FCSTD DOCUMENT  (FreeCAD 0.21R33771 (Git))
Label: StudioPosizioneIngranaggiFilettatura
License: All rights reserved
LicenseURL: http://en.wikipedia.org/wiki/All_rights_reserved
objects: Sketcher::SketchObject×13, PartDesign::Body×1
note: 14 computed .brp shape members not serialized (recipe doc carries the construction recipe); baked Part::Feature solids carry a one-line shape summary decoded from their .brp

FEATURE [Sketcher::SketchObject] Sketch
  FullyConstrained = false
  MapMode = 5
  Support = -> [XY_Plane]
  sketch-geometry (8):
    g0: LineSegment StartX=-130 StartY=161.215 StartZ=0 EndX=-130 EndY=148.136 EndZ=0
    g1: LineSegment StartX=-137.541 StartY=155 StartZ=0 EndX=-124.899 EndY=155 EndZ=0
    g2: Circle CenterX=-130 CenterY=155 CenterZ=0 NormalX=0 NormalY=0 NormalZ=1 AngleXU=0 Radius=17.5
    g3: Circle CenterX=-84.1606 CenterY=129.385 CenterZ=0 NormalX=0 NormalY=0 NormalZ=1 AngleXU=0 Radius=35
    g4: Circle CenterX=-54.3551 CenterY=94.9479 CenterZ=0 NormalX=0 NormalY=0 NormalZ=1 AngleXU=0 Radius=30
    g5: Circle CenterX=0 CenterY=0 CenterZ=0 NormalX=0 NormalY=0 NormalZ=1 AngleXU=0 Radius=16.0185
    g6: Circle CenterX=-84.1606 CenterY=129.385 CenterZ=0 NormalX=0 NormalY=0 NormalZ=1 AngleXU=0 Radius=15
    g7: Circle CenterX=-5.98814 CenterY=50.9759 CenterZ=0 NormalX=0 NormalY=0 NormalZ=1 AngleXU=0 Radius=35
  constraints (13):
    c: Vertical(g0)
    c: Horizontal(g1)
    c: DistanceX(g0,g-1) = 130
    c: PointOnObject(g2,g0)
    c: DistanceY(g-1,g1) = 155
    c: PointOnObject(g2,g1)
    c: Radius(g2) = 17.5
    c: Radius(g3) = 35
    c: Coincident(g5,g-1)
    c: Coincident(g6,g3)
    c: Radius(g6) = 15
    c: Radius(g4) = 30
    c: Radius(g7) = 35
FEATURE [Sketcher::SketchObject] Sketch001  label="Sketch0_2"
  FullyConstrained = false
  MapMode = 5
  sketch-geometry (10):
    g0: LineSegment StartX=-130 StartY=161.215 StartZ=0 EndX=-130 EndY=148.136 EndZ=0
    g1: LineSegment StartX=-137.541 StartY=155 StartZ=0 EndX=-124.899 EndY=155 EndZ=0
    g2: Circle CenterX=-130 CenterY=155 CenterZ=0 NormalX=0 NormalY=0 NormalZ=1 AngleXU=0 Radius=22
    g3: Circle CenterX=-79.8283 CenterY=111.953 CenterZ=0 NormalX=0 NormalY=0 NormalZ=1 AngleXU=0 Radius=44
    g4: Circle CenterX=-54.5871 CenterY=76.5539 CenterZ=0 NormalX=0 NormalY=0 NormalZ=1 AngleXU=0 Radius=31.25
    g5: Circle CenterX=0 CenterY=0 CenterZ=0 NormalX=0 NormalY=0 NormalZ=1 AngleXU=0 Radius=19
    g6: Circle CenterX=-79.8283 CenterY=111.953 CenterZ=0 NormalX=0 NormalY=0 NormalZ=1 AngleXU=0 Radius=12.5
    g7: Circle CenterX=-29.1528 CenterY=40.8844 CenterZ=0 NormalX=0 NormalY=0 NormalZ=1 AngleXU=0 Radius=31
    g8: Circle CenterX=-54.5871 CenterY=76.5539 CenterZ=0 NormalX=0 NormalY=0 NormalZ=1 AngleXU=0 Radius=12.5
    g9: LineSegment StartX=-79.8283 StartY=111.953 StartZ=0 EndX=0 EndY=0 EndZ=0
  constraints (20):
    c: Vertical(g0)
    c: Horizontal(g1)
    c: DistanceX(g0,g-1) = 130
    c: PointOnObject(g2,g0)
    c: DistanceY(g-1,g1) = 155
    c: PointOnObject(g2,g1)
    c: Radius(g2) = 22
    c: Radius(g3) = 44
    c: Coincident(g5,g-1)
    c: Coincident(g6,g3)
    c: Radius(g6) = 12.5
    c: Radius(g4) = 31.25
    c: Radius(g7) = 31
    c: Coincident(g8,g4)
    c: Radius(g8) = 12.5
    c: Radius(g5) = 19
    c: Coincident(g9,g3)
    c: Coincident(g9,g5)
    c: PointOnObject(g4,g9)
    c: PointOnObject(g7,g9)
FEATURE [Sketcher::SketchObject] Sketch002  label="Sketch0_25"
  FullyConstrained = false
  MapMode = 5
  sketch-geometry (10):
    g0: LineSegment StartX=-130 StartY=161.215 StartZ=0 EndX=-130 EndY=148.136 EndZ=0
    g1: LineSegment StartX=-137.541 StartY=155 StartZ=0 EndX=-124.899 EndY=155 EndZ=0
    g2: Circle CenterX=-130 CenterY=155 CenterZ=0 NormalX=0 NormalY=0 NormalZ=1 AngleXU=0 Radius=22
    g3: Circle CenterX=-69.3987 CenterY=116.141 CenterZ=0 NormalX=0 NormalY=0 NormalZ=1 AngleXU=0 Radius=50
    g4: Circle CenterX=-36.9263 CenterY=61.7972 CenterZ=0 NormalX=0 NormalY=0 NormalZ=1 AngleXU=0 Radius=44
    g5: Circle CenterX=0 CenterY=0 CenterZ=0 NormalX=0 NormalY=0 NormalZ=1 AngleXU=0 Radius=19
    g6: Circle CenterX=-69.3987 CenterY=116.141 CenterZ=0 NormalX=0 NormalY=0 NormalZ=1 AngleXU=0 Radius=19
    g7: Circle CenterX=-20.1669 CenterY=33.7498 CenterZ=0 NormalX=0 NormalY=0 NormalZ=1 AngleXU=0 Radius=20
    g8: Circle CenterX=-36.9263 CenterY=61.7972 CenterZ=0 NormalX=0 NormalY=0 NormalZ=1 AngleXU=0 Radius=12.5
    g9: LineSegment StartX=-69.3987 StartY=116.141 StartZ=0 EndX=0 EndY=0 EndZ=0
  constraints (21):
    c: Vertical(g0)
    c: Horizontal(g1)
    c: DistanceX(g0,g-1) = 130
    c: PointOnObject(g2,g0)
    c: DistanceY(g-1,g1) = 155
    c: PointOnObject(g2,g1)
    c: Radius(g2) = 22
    c: Radius(g3) = 50
    c: Coincident(g5,g-1)
    c: Coincident(g6,g3)
    c: Radius(g6) = 19
    c: Radius(g4) = 44
    c: Radius(g7) = 20
    c: Coincident(g8,g4)
    c: Radius(g8) = 12.5
    c: Radius(g5) = 19
    c: Coincident(g9,g3)
    c: Coincident(g9,g5)
    c: PointOnObject(g4,g9)
    c: PointOnObject(g7,g9)
    c: Angle(g-1,g9) = 2.1094
FEATURE [Sketcher::SketchObject] Sketch003  label="Sketch0_50"
  FullyConstrained = false
  MapMode = 5
  sketch-geometry (10):
    g0: LineSegment StartX=-130 StartY=161.215 StartZ=0 EndX=-130 EndY=148.136 EndZ=0
    g1: LineSegment StartX=-137.541 StartY=155 StartZ=0 EndX=-124.899 EndY=155 EndZ=0
    g2: Circle CenterX=-130 CenterY=155 CenterZ=0 NormalX=0 NormalY=0 NormalZ=1 AngleXU=0 Radius=22
    g3: Circle CenterX=-65.5057 CenterY=123.377 CenterZ=0 NormalX=0 NormalY=0 NormalZ=1 AngleXU=0 Radius=50
    g4: Circle CenterX=-35.8708 CenterY=67.5609 CenterZ=0 NormalX=0 NormalY=0 NormalZ=1 AngleXU=0 Radius=44
    g5: Circle CenterX=0 CenterY=0 CenterZ=0 NormalX=0 NormalY=0 NormalZ=1 AngleXU=0 Radius=19
    g6: Circle CenterX=-65.5057 CenterY=123.377 CenterZ=0 NormalX=0 NormalY=0 NormalZ=1 AngleXU=0 Radius=19
    g7: Circle CenterX=-35.8708 CenterY=67.5609 CenterZ=0 NormalX=0 NormalY=0 NormalZ=1 AngleXU=0 Radius=25
    g8: LineSegment StartX=-65.5057 StartY=123.377 StartZ=0 EndX=0 EndY=0 EndZ=0
    g9: Circle CenterX=-16.4847 CenterY=31.0482 CenterZ=0 NormalX=0 NormalY=0 NormalZ=1 AngleXU=0 Radius=16
  constraints (20):
    c: Vertical(g0)
    c: Horizontal(g1)
    c: DistanceX(g0,g-1) = 130
    c: PointOnObject(g2,g0)
    c: DistanceY(g-1,g1) = 155
    c: PointOnObject(g2,g1)
    c: Radius(g2) = 22
    c: Radius(g3) = 50
    c: Coincident(g5,g-1)
    c: Coincident(g6,g3)
    c: Radius(g6) = 19
    c: Radius(g4) = 44
    c: Coincident(g7,g4)
    c: Radius(g7) = 25
    c: Radius(g5) = 19
    c: Coincident(g8,g3)
    c: PointOnObject(g4,g8)
    c: Coincident(g8,g5)
    c: PointOnObject(g9,g8)
    c: Radius(g9) = 16
FEATURE [Sketcher::SketchObject] Sketch004  label="Sketch0_75"
  FullyConstrained = false
  MapMode = 5
  sketch-geometry (10):
    g0: LineSegment StartX=-130 StartY=161.215 StartZ=0 EndX=-130 EndY=148.136 EndZ=0
    g1: LineSegment StartX=-137.541 StartY=155 StartZ=0 EndX=-124.899 EndY=155 EndZ=0
    g2: Circle CenterX=-130 CenterY=155 CenterZ=0 NormalX=0 NormalY=0 NormalZ=1 AngleXU=0 Radius=22
    g3: Circle CenterX=-79.3893 CenterY=104.018 CenterZ=0 NormalX=0 NormalY=0 NormalZ=1 AngleXU=0 Radius=50
    g4: Circle CenterX=-51.6904 CenterY=67.7259 CenterZ=0 NormalX=0 NormalY=0 NormalZ=1 AngleXU=0 Radius=26
    g5: Circle CenterX=0 CenterY=0 CenterZ=0 NormalX=0 NormalY=0 NormalZ=1 AngleXU=0 Radius=19
    g6: Circle CenterX=-79.3893 CenterY=104.018 CenterZ=0 NormalX=0 NormalY=0 NormalZ=1 AngleXU=0 Radius=19
    g7: Circle CenterX=-51.6904 CenterY=67.7259 CenterZ=0 NormalX=0 NormalY=0 NormalZ=1 AngleXU=0 Radius=5
    g8: LineSegment StartX=-79.3893 StartY=104.018 StartZ=0 EndX=0 EndY=0 EndZ=0
    g9: Circle CenterX=-23.8875 CenterY=31.2979 CenterZ=0 NormalX=0 NormalY=0 NormalZ=1 AngleXU=0 Radius=20
  constraints (20):
    c: Vertical(g0)
    c: Horizontal(g1)
    c: DistanceX(g0,g-1) = 130
    c: PointOnObject(g2,g0)
    c: DistanceY(g-1,g1) = 155
    c: PointOnObject(g2,g1)
    c: Radius(g2) = 22
    c: Radius(g3) = 50
    c: Coincident(g5,g-1)
    c: Coincident(g6,g3)
    c: Radius(g6) = 19
    c: Radius(g4) = 26
    c: Coincident(g7,g4)
    c: Radius(g7) = 5
    c: Radius(g5) = 19
    c: Coincident(g8,g3)
    c: PointOnObject(g4,g8)
    c: Coincident(g8,g5)
    c: PointOnObject(g9,g8)
    c: Radius(g9) = 20
FEATURE [Sketcher::SketchObject] Sketch005  label="Sketch0_8"
  FullyConstrained = false
  MapMode = 5
  sketch-geometry (10):
    g0: LineSegment StartX=-130 StartY=161.215 StartZ=0 EndX=-130 EndY=148.136 EndZ=0
    g1: LineSegment StartX=-137.541 StartY=155 StartZ=0 EndX=-124.899 EndY=155 EndZ=0
    g2: Circle CenterX=-130 CenterY=155 CenterZ=0 NormalX=0 NormalY=0 NormalZ=1 AngleXU=0 Radius=22
    g3: Circle CenterX=-71.9427 CenterY=124.555 CenterZ=0 NormalX=0 NormalY=0 NormalZ=1 AngleXU=0 Radius=43.75
    g4: Circle CenterX=-50.103 CenterY=86.744 CenterZ=0 NormalX=0 NormalY=0 NormalZ=1 AngleXU=0 Radius=31.25
    g5: Circle CenterX=0 CenterY=0 CenterZ=0 NormalX=0 NormalY=0 NormalZ=1 AngleXU=0 Radius=19
    g6: Circle CenterX=-71.9427 CenterY=124.555 CenterZ=0 NormalX=0 NormalY=0 NormalZ=1 AngleXU=0 Radius=12.5
    g7: Circle CenterX=-50.103 CenterY=86.744 CenterZ=0 NormalX=0 NormalY=0 NormalZ=1 AngleXU=0 Radius=5
    g8: LineSegment StartX=-71.9427 StartY=124.555 StartZ=0 EndX=0 EndY=0 EndZ=0
    g9: Circle CenterX=-21.9555 CenterY=38.012 CenterZ=0 NormalX=0 NormalY=0 NormalZ=1 AngleXU=0 Radius=25
  constraints (20):
    c: Vertical(g0)
    c: Horizontal(g1)
    c: DistanceX(g0,g-1) = 130
    c: PointOnObject(g2,g0)
    c: DistanceY(g-1,g1) = 155
    c: PointOnObject(g2,g1)
    c: Radius(g2) = 22
    c: Radius(g3) = 43.75
    c: Coincident(g5,g-1)
    c: Coincident(g6,g3)
    c: Radius(g6) = 12.5
    c: Radius(g4) = 31.25
    c: Coincident(g7,g4)
    c: Radius(g7) = 5
    c: Radius(g5) = 19
    c: Coincident(g8,g3)
    c: PointOnObject(g4,g8)
    c: Coincident(g8,g5)
    c: PointOnObject(g9,g8)
    c: Radius(g9) = 25
FEATURE [Sketcher::SketchObject] Sketch006  label="Sketch_1_0"
  FullyConstrained = false
  MapMode = 5
  sketch-geometry (10):
    g0: LineSegment StartX=-130 StartY=161.215 StartZ=0 EndX=-130 EndY=148.136 EndZ=0
    g1: LineSegment StartX=-137.541 StartY=155 StartZ=0 EndX=-124.899 EndY=155 EndZ=0
    g2: Circle CenterX=-130 CenterY=155 CenterZ=0 NormalX=0 NormalY=0 NormalZ=1 AngleXU=0 Radius=22
    g3: Circle CenterX=-78.399 CenterY=113.861 CenterZ=0 NormalX=0 NormalY=0 NormalZ=1 AngleXU=0 Radius=43.75
    g4: Circle CenterX=-46.27 CenterY=67.1995 CenterZ=0 NormalX=0 NormalY=0 NormalZ=1 AngleXU=0 Radius=37.5
    g5: Circle CenterX=0 CenterY=-1.42e-14 CenterZ=0 NormalX=0 NormalY=0 NormalZ=1 AngleXU=0 Radius=19
    g6: Circle CenterX=-78.399 CenterY=113.861 CenterZ=0 NormalX=0 NormalY=0 NormalZ=1 AngleXU=0 Radius=18.75
    g7: Circle CenterX=-46.27 CenterY=67.1995 CenterZ=0 NormalX=0 NormalY=0 NormalZ=1 AngleXU=0 Radius=5
    g8: LineSegment StartX=-78.399 StartY=113.861 StartZ=0 EndX=0 EndY=-1.42e-14 EndZ=0
    g9: Circle CenterX=-17.8364 CenterY=25.9045 CenterZ=0 NormalX=0 NormalY=0 NormalZ=1 AngleXU=0 Radius=12.5
  constraints (20):
    c: Vertical(g0)
    c: Horizontal(g1)
    c: DistanceX(g0,g-1) = 130
    c: PointOnObject(g2,g0)
    c: DistanceY(g-1,g1) = 155
    c: PointOnObject(g2,g1)
    c: Radius(g2) = 22
    c: Radius(g3) = 43.75
    c: Coincident(g5,g-1)
    c: Coincident(g6,g3)
    c: Radius(g6) = 18.75
    c: Radius(g4) = 37.5
    c: Coincident(g7,g4)
    c: Radius(g7) = 5
    c: Radius(g5) = 19
    c: Coincident(g8,g3)
    c: PointOnObject(g4,g8)
    c: Coincident(g8,g5)
    c: PointOnObject(g9,g8)
    c: Radius(g9) = 12.5
FEATURE [Sketcher::SketchObject] Sketch007  label="Sketch_1_25"
  FullyConstrained = false
  MapMode = 5
  sketch-geometry (10):
    g0: LineSegment StartX=-130 StartY=161.215 StartZ=0 EndX=-130 EndY=148.136 EndZ=0
    g1: LineSegment StartX=-137.541 StartY=155 StartZ=0 EndX=-124.899 EndY=155 EndZ=0
    g2: Circle CenterX=-130 CenterY=155 CenterZ=0 NormalX=0 NormalY=0 NormalZ=1 AngleXU=0 Radius=22
    g3: Circle CenterX=-68.136 CenterY=133.379 CenterZ=0 NormalX=0 NormalY=0 NormalZ=1 AngleXU=0 Radius=43.75
    g4: Circle CenterX=-38.4892 CenterY=75.3442 CenterZ=0 NormalX=0 NormalY=0 NormalZ=1 AngleXU=0 Radius=40
    g5: Circle CenterX=0 CenterY=0 CenterZ=0 NormalX=0 NormalY=0 NormalZ=1 AngleXU=0 Radius=19
    g6: Circle CenterX=-68.136 CenterY=133.379 CenterZ=0 NormalX=0 NormalY=0 NormalZ=1 AngleXU=0 Radius=25
    g7: Circle CenterX=-38.4892 CenterY=75.3442 CenterZ=0 NormalX=0 NormalY=0 NormalZ=1 AngleXU=0 Radius=5
    g8: LineSegment StartX=-68.136 StartY=133.379 StartZ=0 EndX=0 EndY=0 EndZ=0
    g9: Circle CenterX=-14.3671 CenterY=28.1242 CenterZ=0 NormalX=0 NormalY=0 NormalZ=1 AngleXU=0 Radius=12.5
  constraints (21):
    c: Vertical(g0)
    c: Horizontal(g1)
    c: DistanceX(g0,g-1) = 130
    c: PointOnObject(g2,g0)
    c: DistanceY(g-1,g1) = 155
    c: PointOnObject(g2,g1)
    c: Radius(g2) = 22
    c: Radius(g3) = 43.75
    c: Coincident(g5,g-1)
    c: Coincident(g6,g3)
    c: Radius(g6) = 25
    c: Radius(g4) = 40
    c: Coincident(g7,g4)
    c: Radius(g7) = 5
    c: Radius(g5) = 19
    c: Coincident(g8,g3)
    c: PointOnObject(g4,g8)
    c: Coincident(g8,g5)
    c: PointOnObject(g9,g8)
    c: Radius(g9) = 12.5
    c: Angle(g-1,g8) = 2.04308
FEATURE [Sketcher::SketchObject] Sketch008  label="Sketch_1_5"
  FullyConstrained = false
  MapMode = 5
  sketch-geometry (10):
    g0: LineSegment StartX=-130 StartY=161.215 StartZ=0 EndX=-130 EndY=148.136 EndZ=0
    g1: LineSegment StartX=-137.541 StartY=155 StartZ=0 EndX=-124.899 EndY=155 EndZ=0
    g2: Circle CenterX=-130 CenterY=155 CenterZ=0 NormalX=0 NormalY=0 NormalZ=1 AngleXU=0 Radius=22
    g3: Circle CenterX=-74.8165 CenterY=119.731 CenterZ=0 NormalX=0 NormalY=0 NormalZ=1 AngleXU=0 Radius=43.75
    g4: Circle CenterX=-42.4917 CenterY=68.0009 CenterZ=0 NormalX=0 NormalY=0 NormalZ=1 AngleXU=0 Radius=35
    g5: Circle CenterX=0 CenterY=0 CenterZ=0 NormalX=0 NormalY=0 NormalZ=1 AngleXU=0 Radius=19
    g6: Circle CenterX=-74.8165 CenterY=119.731 CenterZ=0 NormalX=0 NormalY=0 NormalZ=1 AngleXU=0 Radius=26.25
    g7: Circle CenterX=-42.4917 CenterY=68.0009 CenterZ=0 NormalX=0 NormalY=0 NormalZ=1 AngleXU=0 Radius=5
    g8: LineSegment StartX=-74.8165 StartY=119.731 StartZ=0 EndX=0 EndY=0 EndZ=0
    g9: Circle CenterX=-17.0877 CenterY=27.3461 CenterZ=0 NormalX=0 NormalY=0 NormalZ=1 AngleXU=0 Radius=12.5
  constraints (21):
    c: Vertical(g0)
    c: Horizontal(g1)
    c: DistanceX(g0,g-1) = 130
    c: PointOnObject(g2,g0)
    c: DistanceY(g-1,g1) = 155
    c: PointOnObject(g2,g1)
    c: Radius(g2) = 22
    c: Radius(g3) = 43.75
    c: Coincident(g5,g-1)
    c: Coincident(g6,g3)
    c: Radius(g6) = 26.25
    c: Radius(g4) = 35
    c: Coincident(g7,g4)
    c: Radius(g7) = 5
    c: Radius(g5) = 19
    c: Coincident(g8,g3)
    c: PointOnObject(g4,g8)
    c: Coincident(g8,g5)
    c: PointOnObject(g9,g8)
    c: Radius(g9) = 12.5
    c: Angle(g-1,g8) = 2.1293
FEATURE [Sketcher::SketchObject] Sketch009  label="Sketch_1_75"
  FullyConstrained = false
  MapMode = 5
  sketch-geometry (10):
    g0: LineSegment StartX=-130 StartY=161.215 StartZ=0 EndX=-130 EndY=148.136 EndZ=0
    g1: LineSegment StartX=-137.541 StartY=155 StartZ=0 EndX=-124.899 EndY=155 EndZ=0
    g2: Circle CenterX=-130 CenterY=155 CenterZ=0 NormalX=0 NormalY=0 NormalZ=1 AngleXU=0 Radius=22
    g3: Circle CenterX=-82.8744 CenterY=118.357 CenterZ=0 NormalX=0 NormalY=0 NormalZ=1 AngleXU=0 Radius=37.5
    g4: Circle CenterX=-48.7733 CenterY=69.6555 CenterZ=0 NormalX=0 NormalY=0 NormalZ=1 AngleXU=0 Radius=40
    g5: Circle CenterX=0 CenterY=0 CenterZ=0 NormalX=0 NormalY=0 NormalZ=1 AngleXU=0 Radius=19
    g6: Circle CenterX=-82.8744 CenterY=118.357 CenterZ=0 NormalX=0 NormalY=0 NormalZ=1 AngleXU=0 Radius=18.75
    g7: Circle CenterX=-48.7733 CenterY=69.6555 CenterZ=0 NormalX=0 NormalY=0 NormalZ=1 AngleXU=0 Radius=5
    g8: LineSegment StartX=-82.8744 StartY=118.357 StartZ=0 EndX=0 EndY=0 EndZ=0
    g9: Circle CenterX=-18.361 CenterY=26.2222 CenterZ=0 NormalX=0 NormalY=0 NormalZ=1 AngleXU=0 Radius=12.5
  constraints (21):
    c: Vertical(g0)
    c: Horizontal(g1)
    c: DistanceX(g0,g-1) = 130
    c: PointOnObject(g2,g0)
    c: DistanceY(g-1,g1) = 155
    c: PointOnObject(g2,g1)
    c: Radius(g2) = 22
    c: Radius(g3) = 37.5
    c: Coincident(g5,g-1)
    c: Coincident(g6,g3)
    c: Radius(g6) = 18.75
    c: Radius(g4) = 40
    c: Coincident(g7,g4)
    c: Radius(g7) = 5
    c: Radius(g5) = 19
    c: Coincident(g8,g3)
    c: PointOnObject(g4,g8)
    c: Coincident(g8,g5)
    c: PointOnObject(g9,g8)
    c: Radius(g9) = 12.5
    c: Angle(g-1,g8) = 2.18166
FEATURE [Sketcher::SketchObject] Sketch010  label="Sketch_2_0"
  FullyConstrained = false
  MapMode = 5
  sketch-geometry (10):
    g0: LineSegment StartX=-130 StartY=161.215 StartZ=0 EndX=-130 EndY=148.136 EndZ=0
    g1: LineSegment StartX=-137.541 StartY=155 StartZ=0 EndX=-124.899 EndY=155 EndZ=0
    g2: Circle CenterX=-130 CenterY=155 CenterZ=0 NormalX=0 NormalY=0 NormalZ=1 AngleXU=0 Radius=22
    g3: Circle CenterX=-74.7681 CenterY=119.654 CenterZ=0 NormalX=0 NormalY=0 NormalZ=1 AngleXU=0 Radius=43.75
    g4: Circle CenterX=-48.1 CenterY=76.9761 CenterZ=0 NormalX=0 NormalY=0 NormalZ=1 AngleXU=0 Radius=26.25
    g5: Circle CenterX=0 CenterY=0 CenterZ=0 NormalX=0 NormalY=0 NormalZ=1 AngleXU=0 Radius=19
    g6: Circle CenterX=-74.7681 CenterY=119.654 CenterZ=0 NormalX=0 NormalY=0 NormalZ=1 AngleXU=0 Radius=25
    g7: Circle CenterX=-48.1 CenterY=76.9761 CenterZ=0 NormalX=0 NormalY=0 NormalZ=1 AngleXU=0 Radius=5
    g8: LineSegment StartX=-74.7681 StartY=119.654 StartZ=0 EndX=0 EndY=0 EndZ=0
    g9: Circle CenterX=-21.9262 CenterY=35.0892 CenterZ=0 NormalX=0 NormalY=0 NormalZ=1 AngleXU=0 Radius=22.5
  constraints (21):
    c: Vertical(g0)
    c: Horizontal(g1)
    c: DistanceX(g0,g-1) = 130
    c: PointOnObject(g2,g0)
    c: DistanceY(g-1,g1) = 155
    c: PointOnObject(g2,g1)
    c: Radius(g2) = 22
    c: Radius(g3) = 43.75
    c: Coincident(g5,g-1)
    c: Coincident(g6,g3)
    c: Radius(g6) = 25
    c: Radius(g4) = 26.25
    c: Coincident(g7,g4)
    c: Radius(g7) = 5
    c: Radius(g5) = 19
    c: Coincident(g8,g3)
    c: PointOnObject(g4,g8)
    c: Coincident(g8,g5)
    c: PointOnObject(g9,g8)
    c: Radius(g9) = 22.5
    c: Angle(g-1,g8) = 2.1293
FEATURE [Sketcher::SketchObject] Sketch011  label="Sketch_2_25"
  FullyConstrained = false
  MapMode = 5
  sketch-geometry (10):
    g0: LineSegment StartX=-130 StartY=161.215 StartZ=0 EndX=-130 EndY=148.136 EndZ=0
    g1: LineSegment StartX=-137.541 StartY=155 StartZ=0 EndX=-124.899 EndY=155 EndZ=0
    g2: Circle CenterX=-130 CenterY=155 CenterZ=0 NormalX=0 NormalY=0 NormalZ=1 AngleXU=0 Radius=22
    g3: Circle CenterX=-83.8891 CenterY=117.608 CenterZ=0 NormalX=0 NormalY=0 NormalZ=1 AngleXU=0 Radius=37.5
    g4: Circle CenterX=-59.2637 CenterY=83.0847 CenterZ=0 NormalX=0 NormalY=0 NormalZ=1 AngleXU=0 Radius=20
    g5: Circle CenterX=0 CenterY=0 CenterZ=0 NormalX=0 NormalY=0 NormalZ=1 AngleXU=0 Radius=19
    g6: Circle CenterX=-83.8891 CenterY=117.608 CenterZ=0 NormalX=0 NormalY=0 NormalZ=1 AngleXU=0 Radius=22.5
    g7: Circle CenterX=-59.2637 CenterY=83.0847 CenterZ=0 NormalX=0 NormalY=0 NormalZ=1 AngleXU=0 Radius=3
    g8: LineSegment StartX=-83.8891 StartY=117.608 StartZ=0 EndX=0 EndY=0 EndZ=0
    g9: Circle CenterX=-29.2925 CenterY=41.0666 CenterZ=0 NormalX=0 NormalY=0 NormalZ=1 AngleXU=0 Radius=31.25
  constraints (21):
    c: Vertical(g0)
    c: Horizontal(g1)
    c: DistanceX(g0,g-1) = 130
    c: PointOnObject(g2,g0)
    c: DistanceY(g-1,g1) = 155
    c: PointOnObject(g2,g1)
    c: Radius(g2) = 22
    c: Radius(g3) = 37.5
    c: Coincident(g5,g-1)
    c: Coincident(g6,g3)
    c: Radius(g6) = 22.5
    c: Radius(g4) = 20
    c: Coincident(g7,g4)
    c: Radius(g7) = 3
    c: Radius(g5) = 19
    c: Coincident(g8,g3)
    c: PointOnObject(g4,g8)
    c: Coincident(g8,g5)
    c: PointOnObject(g9,g8)
    c: Radius(g9) = 31.25
    c: Angle(g-1,g8) = 2.19039
FEATURE [Sketcher::SketchObject] Sketch012  label="Sketch_2_5"
  FullyConstrained = false
  MapMode = 5
  sketch-geometry (10):
    g0: LineSegment StartX=-130 StartY=161.215 StartZ=0 EndX=-130 EndY=148.136 EndZ=0
    g1: LineSegment StartX=-137.541 StartY=155 StartZ=0 EndX=-124.899 EndY=155 EndZ=0
    g2: Circle CenterX=-130 CenterY=155 CenterZ=0 NormalX=0 NormalY=0 NormalZ=1 AngleXU=0 Radius=22
    g3: Circle CenterX=-79.6312 CenterY=122.621 CenterZ=0 NormalX=0 NormalY=0 NormalZ=1 AngleXU=0 Radius=37.5
    g4: Circle CenterX=-55.1353 CenterY=84.9009 CenterZ=0 NormalX=0 NormalY=0 NormalZ=1 AngleXU=0 Radius=20
    g5: Circle CenterX=0 CenterY=0 CenterZ=0 NormalX=0 NormalY=0 NormalZ=1 AngleXU=0 Radius=19
    g6: Circle CenterX=-79.6312 CenterY=122.621 CenterZ=0 NormalX=0 NormalY=0 NormalZ=1 AngleXU=0 Radius=25
    g7: Circle CenterX=-55.1353 CenterY=84.9009 CenterZ=0 NormalX=0 NormalY=0 NormalZ=1 AngleXU=0 Radius=3
    g8: LineSegment StartX=-79.6312 StartY=122.621 StartZ=0 EndX=0 EndY=0 EndZ=0
    g9: Circle CenterX=-27.2777 CenterY=42.0041 CenterZ=0 NormalX=0 NormalY=0 NormalZ=1 AngleXU=0 Radius=31.25
  constraints (21):
    c: Vertical(g0)
    c: Horizontal(g1)
    c: DistanceX(g0,g-1) = 130
    c: PointOnObject(g2,g0)
    c: DistanceY(g-1,g1) = 155
    c: PointOnObject(g2,g1)
    c: Radius(g2) = 22
    c: Radius(g3) = 37.5
    c: Coincident(g5,g-1)
    c: Coincident(g6,g3)
    c: Radius(g6) = 25
    c: Radius(g4) = 20
    c: Coincident(g7,g4)
    c: Radius(g7) = 3
    c: Radius(g5) = 19
    c: Coincident(g8,g3)
    c: PointOnObject(g4,g8)
    c: Coincident(g8,g5)
    c: PointOnObject(g9,g8)
    c: Radius(g9) = 31.25
    c: Angle(g-1,g8) = 2.14675
FEATURE [PartDesign::Body] Body
  Group = -> [Sketch,Sketch001,Sketch002,Sketch003,Sketch004,Sketch005,Sketch006,Sketch007,Sketch008,Sketch009,Sketch010,Sketch011,Sketch012]
  Origin = -> Origin
